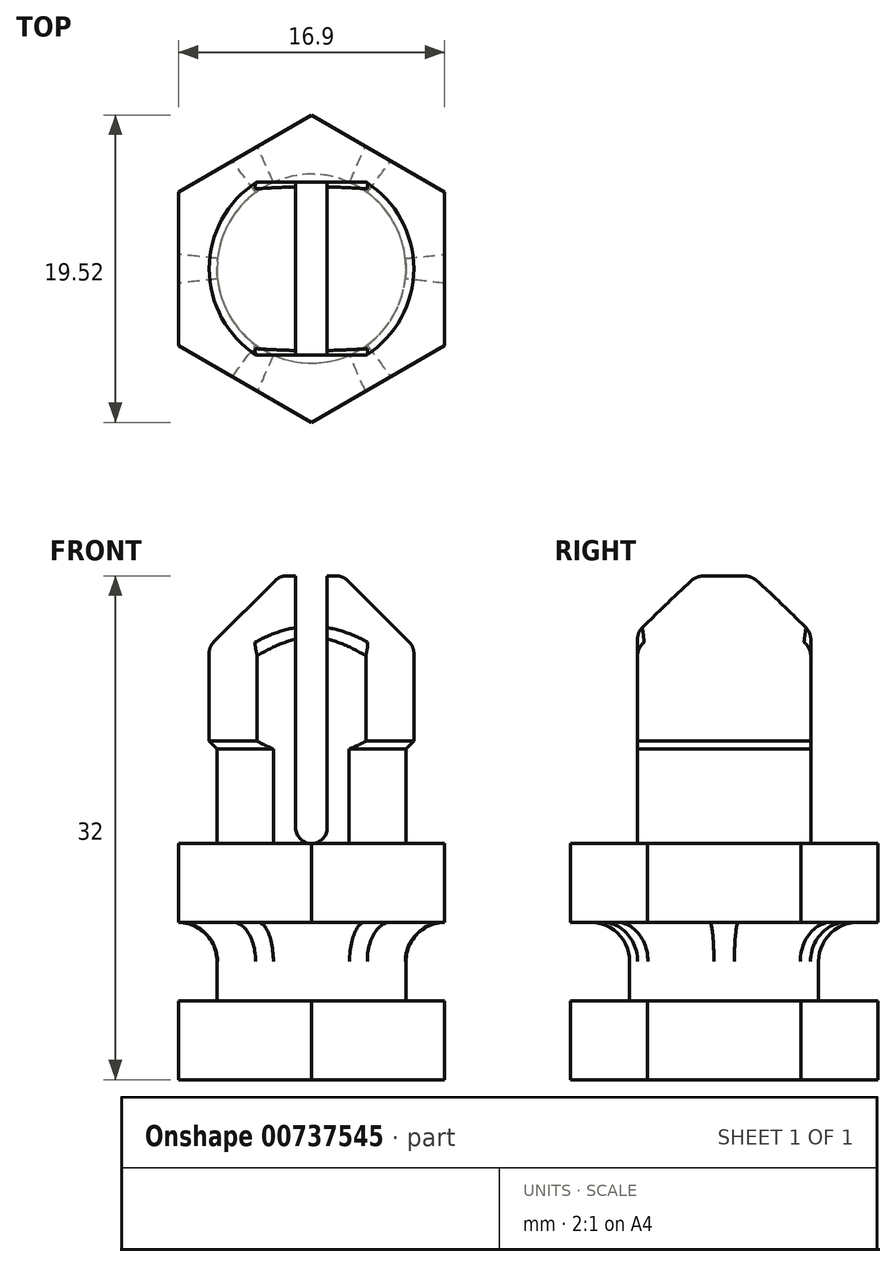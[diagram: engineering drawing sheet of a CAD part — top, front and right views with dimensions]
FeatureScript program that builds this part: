
annotation { "Feature Type Name" : "Feature", "Feature Type Description" : "" }
export const myFeature = defineFeature(function(context is Context, id is Id, definition is map)
    precondition{}
    {
        {
            var Q0;
            Q0=qCreatedBy(makeId("Top.planeOp"),FACE);
            var sketch = newSketch(context, id + "F0", { "sketchPlane" : qUnion([Q0])});
            skCircle(sketch, "E0.cCircle", {"center": v(0, 0) * mm, "radius": 9.76 * mm, "construction": true});
            skLineSegment(sketch, "E0.0", {"start": v(0, 9.76) * mm, "end": v(8.45, 4.88) * mm});
            skLineSegment(sketch, "E0.1", {"start": v(8.45, 4.88) * mm, "end": v(8.45, -4.88) * mm});
            skLineSegment(sketch, "E0.2", {"start": v(8.45, -4.88) * mm, "end": v(0, -9.76) * mm});
            skLineSegment(sketch, "E0.3", {"start": v(0, -9.76) * mm, "end": v(-8.45, -4.88) * mm});
            skLineSegment(sketch, "E0.4", {"start": v(-8.45, -4.88) * mm, "end": v(-8.45, 4.88) * mm});
            skLineSegment(sketch, "E0.5", {"start": v(-8.45, 4.88) * mm, "end": v(0, 9.76) * mm});
            skCircle(sketch, "E1", {"center": v(0, 0) * mm, "radius": 6 * mm});
            skSolve(sketch);
        }
        {
            var Q0;
            Q0=makeQuery(id+"F0.imprint","IMPRINT",FACE,{"disambiguationData":[TD([[makeQuery(id+"F0.imprint","IMPRINT",EDGE,{"derivedFrom":sQuery(id+"F0.wireOp",EDGE,"E1")}),1.0]])]});
            extrude(context, id + "F1", {"entities" : qUnion([Q0]), "depth" : 13 * mm, "offsetDistance" : 25 * mm});
        }
        {
            var Q0;
            Q0=makeQuery(id+"F0.imprint","IMPRINT",FACE,{"disambiguationData":[TD([[makeQuery(id+"F0.imprint","IMPRINT",EDGE,{"derivedFrom":sQuery(id+"F0.wireOp",EDGE,"E0.0")}),-1.0]])]});
            var Q1;
            Q1=makeQuery(id+"F1.opExtrude","CAP_FACE",FACE,{"disambiguationData":[OSD([sQuery(id+"F0.wireOp",EDGE,"E1")])],"isStart":true});
            extrude(context, id + "F2", {"entities" : qUnion([Q0, Q1]), "operationType" : NewBodyOperationType.ADD, "oppositeDirection" : true, "depth" : 5 * mm, "offsetDistance" : 25 * mm});
        }
        {
            var Q0;
            Q0=qCreatedBy(makeId("Front.planeOp"),FACE);
            var sketch = newSketch(context, id + "F3", { "sketchPlane" : qUnion([Q0])});
            skLineSegment(sketch, "E2", {"start": v(0, 0) * mm, "end": v(-6.5, 6.5) * mm});
            skLineSegment(sketch, "E3", {"start": v(-6.5, 6.5) * mm, "end": v(-6.5, 12.5) * mm});
            skLineSegment(sketch, "E4", {"start": v(-6.5, 12.5) * mm, "end": v(-2, 17) * mm});
            skLineSegment(sketch, "E5", {"start": v(-2, 17) * mm, "end": v(0, 17) * mm});
            skLineSegment(sketch, "E6", {"start": v(0, 17) * mm, "end": v(0, 0) * mm});
            skLineSegment(sketch, "E7", {"start": v(0, 0) * mm, "end": v(0, 18.61) * mm, "construction": true});
            skSolve(sketch);
        }
        {
            var Q0;
            Q0=qSketchRegion(id+"F3",true);
            var Q1;
            Q1=sQuery(id+"F3.wireOp",EDGE,"E7");
            revolve(context, id + "F4", {"operationType" : NewBodyOperationType.ADD, "surfaceOperationType" : NewSurfaceOperationType.NEW, "entities" : qUnion([Q0]), "axis" : qUnion([Q1]), "revolveType" : RevolveType.FULL});
        }
        {
            var Q0;
            Q0=makeQuery(id+"F4.opRevolve","SWEPT_FACE",FACE,{"disambiguationData":[OSD([sQuery(id+"F3.wireOp",EDGE,"E5")])]});
            var sketch = newSketch(context, id + "F5", { "sketchPlane" : qUnion([Q0])});
            skLineSegment(sketch, "E8.left", {"start": v(-1, 5.5) * mm, "end": v(-1, -5.5) * mm});
            skLineSegment(sketch, "E8.right", {"start": v(1, 5.5) * mm, "end": v(1, -5.5) * mm});
            skLineSegment(sketch, "E9.bottom", {"start": v(12.2, 5.5) * mm, "end": v(1, 5.5) * mm});
            skLineSegment(sketch, "E9.top", {"start": v(12.2, 9.85) * mm, "end": v(-10.35, 9.85) * mm});
            skLineSegment(sketch, "E9.left", {"start": v(12.2, 5.5) * mm, "end": v(12.2, 9.85) * mm});
            skLineSegment(sketch, "E9.right", {"start": v(-10.35, 5.5) * mm, "end": v(-10.35, 9.85) * mm});
            skLineSegment(sketch, "E10.bottom", {"start": v(-10.49, -5.5) * mm, "end": v(-1, -5.5) * mm});
            skLineSegment(sketch, "E10.top", {"start": v(-10.49, -9.75) * mm, "end": v(10.2, -9.75) * mm});
            skLineSegment(sketch, "E10.left", {"start": v(-10.49, -5.5) * mm, "end": v(-10.49, -9.75) * mm});
            skLineSegment(sketch, "E10.right", {"start": v(10.2, -5.5) * mm, "end": v(10.2, -9.75) * mm});
            skLineSegment(sketch, "E11.trimOffspring", {"start": v(-1, 5.5) * mm, "end": v(-10.35, 5.5) * mm});
            skPoint(sketch, "E12.end.orphan", {"position": v(5.15, 6) * mm});
            skPoint(sketch, "E13.end.orphan", {"position": v(0, 6) * mm});
            skLineSegment(sketch, "E14.trimOffspring", {"start": v(1, -5.5) * mm, "end": v(10.2, -5.5) * mm});
            skPoint(sketch, "E15.orphan", {"position": v(6.45, -6) * mm});
            skPoint(sketch, "E16.end.orphan", {"position": v(0, -6) * mm});
            skLineSegment(sketch, "E17", {"start": v(0, 0) * mm, "end": v(-1, 0) * mm, "construction": true});
            skSolve(sketch);
        }
        {
            var Q0;
            {var subQ0=sQuery(id+"F5.wireOp",EDGE,"E10.bottom");Q0=makeQuery(id+"F5.imprint","IMPRINT",FACE,{"disambiguationData":[TD([[makeQuery(id+"F5.imprint","IMPRINT",EDGE,{"derivedFrom":subQ0}),-1.0]])]});}
            var Q1;
            {var subQ4=sQuery(id+"F5.wireOp",EDGE,"E8.left");Q1=makeQuery(id+"F5.imprint","IMPRINT",FACE,{"disambiguationData":[TD([[makeQuery(id+"F5.imprint","IMPRINT",EDGE,{"derivedFrom":subQ4}),1.0]])]});}
            var Q2;
            Q2=makeQuery(id+"F5.imprint","IMPRINT",FACE,{"disambiguationData":[TD([[makeQuery(id+"F5.imprint","IMPRINT",EDGE,{"derivedFrom":sQuery(id+"F5.wireOp",EDGE,"E9.top")}),1.0]])]});
            var Q3;
            {var subQ0=sQuery(id+"F0.wireOp",EDGE,"E1");Q3=makeQuery(id+"F2.boolean.opBoolean","MERGE",FACE,{"derivedFrom":[makeQuery(id+"F2.opExtrude","CAP_FACE",FACE,{"disambiguationData":[OSD([sQuery(id+"F0.wireOp",EDGE,"E0.0"),sQuery(id+"F0.wireOp",EDGE,"E0.1"),sQuery(id+"F0.wireOp",EDGE,"E0.2"),sQuery(id+"F0.wireOp",EDGE,"E0.3"),sQuery(id+"F0.wireOp",EDGE,"E0.4"),sQuery(id+"F0.wireOp",EDGE,"E0.5"),subQ0])],"isStart":true}),makeQuery(id+"F2.opExtrude","CAP_FACE",FACE,{"disambiguationData":[OSD([subQ0])],"isStart":true})]});}
            extrude(context, id + "F6", {"entities" : qUnion([Q0, Q1, Q2]), "operationType" : NewBodyOperationType.REMOVE, "endBound" : BoundingType.UP_TO_SURFACE, "oppositeDirection" : true, "depth" : 25 * mm, "endBoundEntityFace" : qUnion([Q3]), "offsetDistance" : 25 * mm});
        }
        {
            var Q0;
            Q0=makeQuery(id+"F6.boolean.opBoolean","COPY",EDGE,{"derivedFrom":makeQuery(id+"F6.opExtrude","CAP_EDGE",EDGE,{"disambiguationData":[OSD([sQuery(id+"F5.wireOp",EDGE,"E8.left")])],"isStart":false})});
            var Q1;
            Q1=makeQuery(id+"F6.boolean.opBoolean","COPY",EDGE,{"derivedFrom":makeQuery(id+"F6.opExtrude","CAP_EDGE",EDGE,{"disambiguationData":[OSD([sQuery(id+"F5.wireOp",EDGE,"E8.right")])],"isStart":false})});
            var Q2;
            {var subQ0=sQuery(id+"F3.wireOp",EDGE,"E3");var subQ1=sQuery(id+"F3.wireOp",EDGE,"E4");Q2=makeQuery(id+"F6.boolean.opBoolean","SPLIT",EDGE,{"disambiguationData":[TD([makeQuery(id+"F6.opExtrude","SWEPT_FACE",FACE,{"disambiguationData":[OSD([sQuery(id+"F5.wireOp",EDGE,"E10.bottom")])]})])],"derivedFrom":makeQuery(id+"F4.opRevolve","SWEPT_EDGE",EDGE,{"disambiguationData":[OSD([subQ0,subQ1])]})});}
            var Q3;
            {var subQ0=sQuery(id+"F3.wireOp",EDGE,"E3");var subQ1=sQuery(id+"F3.wireOp",EDGE,"E4");Q3=makeQuery(id+"F6.boolean.opBoolean","SPLIT",EDGE,{"disambiguationData":[TD([makeQuery(id+"F6.opExtrude","SWEPT_FACE",FACE,{"disambiguationData":[OSD([sQuery(id+"F5.wireOp",EDGE,"E9.bottom")])]})])],"derivedFrom":makeQuery(id+"F4.opRevolve","SWEPT_EDGE",EDGE,{"disambiguationData":[OSD([subQ0,subQ1])]})});}
            var Q4;
            Q4=makeQuery(id+"F6.boolean.opBoolean","INTERSECT",EDGE,{"derivedFrom":[makeQuery(id+"F4.opRevolve","SWEPT_FACE",FACE,{"disambiguationData":[OSD([sQuery(id+"F3.wireOp",EDGE,"E4")])]}),makeQuery(id+"F6.opExtrude","SWEPT_FACE",FACE,{"disambiguationData":[OSD([sQuery(id+"F5.wireOp",EDGE,"E14.trimOffspring")])]})]});
            var Q5;
            Q5=makeQuery(id+"F6.boolean.opBoolean","INTERSECT",EDGE,{"derivedFrom":[makeQuery(id+"F4.opRevolve","SWEPT_FACE",FACE,{"disambiguationData":[OSD([sQuery(id+"F3.wireOp",EDGE,"E4")])]}),makeQuery(id+"F6.opExtrude","SWEPT_FACE",FACE,{"disambiguationData":[OSD([sQuery(id+"F5.wireOp",EDGE,"E10.bottom")])]})]});
            var Q6;
            Q6=makeQuery(id+"F6.boolean.opBoolean","INTERSECT",EDGE,{"derivedFrom":[makeQuery(id+"F4.opRevolve","SWEPT_FACE",FACE,{"disambiguationData":[OSD([sQuery(id+"F3.wireOp",EDGE,"E4")])]}),makeQuery(id+"F6.opExtrude","SWEPT_FACE",FACE,{"disambiguationData":[OSD([sQuery(id+"F5.wireOp",EDGE,"E11.trimOffspring")])]})]});
            var Q7;
            Q7=makeQuery(id+"F6.boolean.opBoolean","INTERSECT",EDGE,{"derivedFrom":[makeQuery(id+"F4.opRevolve","SWEPT_FACE",FACE,{"disambiguationData":[OSD([sQuery(id+"F3.wireOp",EDGE,"E4")])]}),makeQuery(id+"F6.opExtrude","SWEPT_FACE",FACE,{"disambiguationData":[OSD([sQuery(id+"F5.wireOp",EDGE,"E9.bottom")])]})]});
            var Q8;
            {var subQ0=sQuery(id+"F3.wireOp",EDGE,"E4");var subQ1=sQuery(id+"F3.wireOp",EDGE,"E5");Q8=makeQuery(id+"F6.boolean.opBoolean","SPLIT",EDGE,{"disambiguationData":[TD([makeQuery(id+"F6.opExtrude","SWEPT_FACE",FACE,{"disambiguationData":[OSD([sQuery(id+"F5.wireOp",EDGE,"E8.left")])]})])],"derivedFrom":makeQuery(id+"F4.opRevolve","SWEPT_EDGE",EDGE,{"disambiguationData":[OSD([subQ0,subQ1])]})});}
            var Q9;
            {var subQ0=sQuery(id+"F3.wireOp",EDGE,"E4");var subQ1=sQuery(id+"F3.wireOp",EDGE,"E5");Q9=makeQuery(id+"F6.boolean.opBoolean","SPLIT",EDGE,{"disambiguationData":[TD([makeQuery(id+"F6.opExtrude","SWEPT_FACE",FACE,{"disambiguationData":[OSD([sQuery(id+"F5.wireOp",EDGE,"E8.right")])]})])],"derivedFrom":makeQuery(id+"F4.opRevolve","SWEPT_EDGE",EDGE,{"disambiguationData":[OSD([subQ0,subQ1])]})});}
            fillet(context, id + "F7", {"entities" : qUnion([Q0, Q1, Q2, Q3, Q4, Q5, Q6, Q7, Q8, Q9]), "radius" : 1 * mm, "tangentPropagation" : true, "allowEdgeOverflow" : false});
        }
        {
            var Q0;
            Q0=makeQuery(id+"F0.imprint","IMPRINT",FACE,{"disambiguationData":[TD([[makeQuery(id+"F0.imprint","IMPRINT",EDGE,{"derivedFrom":sQuery(id+"F0.wireOp",EDGE,"E1")}),1.0]])]});
            extrude(context, id + "F8", {"entities" : qUnion([Q0]), "operationType" : NewBodyOperationType.ADD, "oppositeDirection" : true, "depth" : 10 * mm, "offsetDistance" : 25 * mm});
        }
        {
            var Q0;
            Q0=makeQuery(id+"F8.opExtrude","CAP_FACE",FACE,{"disambiguationData":[OSD([sQuery(id+"F0.wireOp",EDGE,"E1")])],"isStart":false});
            var sketch = newSketch(context, id + "F9", { "sketchPlane" : qUnion([Q0])});
            skCircle(sketch, "E18.cCircle", {"center": v(0, 0) * mm, "radius": 9.76 * mm, "construction": true});
            skLineSegment(sketch, "E18.0", {"start": v(0, 9.76) * mm, "end": v(8.45, 4.88) * mm});
            skLineSegment(sketch, "E18.1", {"start": v(8.45, 4.88) * mm, "end": v(8.45, -4.88) * mm});
            skLineSegment(sketch, "E18.2", {"start": v(8.45, -4.88) * mm, "end": v(0, -9.76) * mm});
            skLineSegment(sketch, "E18.3", {"start": v(0, -9.76) * mm, "end": v(-8.45, -4.88) * mm});
            skLineSegment(sketch, "E18.4", {"start": v(-8.45, -4.88) * mm, "end": v(-8.45, 4.88) * mm});
            skLineSegment(sketch, "E18.5", {"start": v(-8.45, 4.88) * mm, "end": v(0, 9.76) * mm});
            skCircle(sketch, "E19", {"center": v(0, 0) * mm, "radius": 6 * mm});
            skSolve(sketch);
        }
        {
            var Q0;
            Q0=makeQuery(id+"F9.imprint","IMPRINT",FACE,{"disambiguationData":[TD([[makeQuery(id+"F9.imprint","IMPRINT",EDGE,{"derivedFrom":sQuery(id+"F9.wireOp",EDGE,"E18.0")}),-1.0]])]});
            var Q1;
            Q1=makeQuery(id+"F9.imprint","IMPRINT",FACE,{"disambiguationData":[TD([[makeQuery(id+"F9.imprint","IMPRINT",EDGE,{"derivedFrom":sQuery(id+"F9.wireOp",EDGE,"E19")}),-1.0]])]});
            extrude(context, id + "F10", {"entities" : qUnion([Q0, Q1]), "operationType" : NewBodyOperationType.ADD, "depth" : 5 * mm, "offsetDistance" : 25 * mm});
        }
        {
            var Q0;
            Q0=makeQuery(id+"F8.opExtrude","CAP_EDGE",EDGE,{"disambiguationData":[OSD([sQuery(id+"F0.wireOp",EDGE,"E1")])],"isStart":false});
            var Q1;
            {var subQ0=sQuery(id+"F0.wireOp",EDGE,"E1");Q1=makeQuery(id+"F8.boolean.opBoolean","INTERSECT",EDGE,{"derivedFrom":[makeQuery(id+"F2.boolean.opBoolean","MERGE",FACE,{"derivedFrom":[makeQuery(id+"F2.opExtrude","CAP_FACE",FACE,{"disambiguationData":[OSD([sQuery(id+"F0.wireOp",EDGE,"E0.0"),sQuery(id+"F0.wireOp",EDGE,"E0.1"),sQuery(id+"F0.wireOp",EDGE,"E0.2"),sQuery(id+"F0.wireOp",EDGE,"E0.3"),sQuery(id+"F0.wireOp",EDGE,"E0.4"),sQuery(id+"F0.wireOp",EDGE,"E0.5"),subQ0])],"isStart":false}),makeQuery(id+"F2.opExtrude","CAP_FACE",FACE,{"disambiguationData":[OSD([subQ0])],"isStart":false})]}),makeQuery(id+"F8.opExtrude","SWEPT_FACE",FACE,{"disambiguationData":[OSD([subQ0])]})]});}
            fillet(context, id + "F11", {"entities" : qUnion([Q0, Q1]), "radius" : 2.5 * mm, "tangentPropagation" : true, "allowEdgeOverflow" : false});
        }
    });
